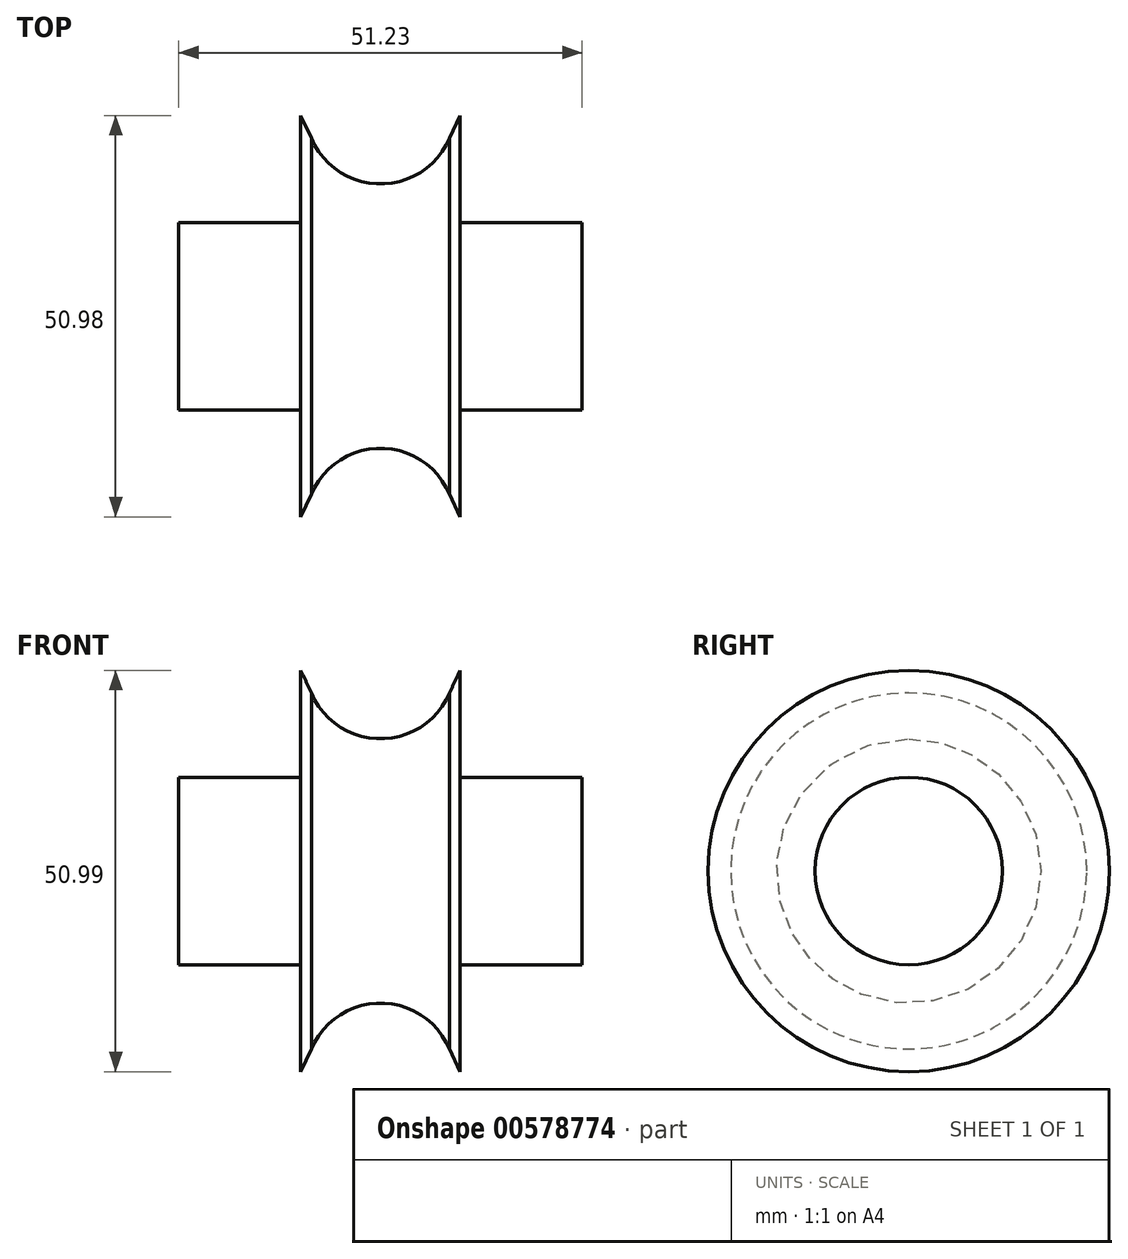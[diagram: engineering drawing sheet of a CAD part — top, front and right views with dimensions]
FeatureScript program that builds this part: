
annotation { "Feature Type Name" : "Feature", "Feature Type Description" : "" }
export const myFeature = defineFeature(function(context is Context, id is Id, definition is map)
    precondition{}
    {
        {
            var Q0;
            Q0=qCreatedBy(makeId("Front.planeOp"),FACE);
            var sketch = newSketch(context, id + "F0", { "sketchPlane" : qUnion([Q0])});
            skLineSegment(sketch, "E0", {"start": v(-30.72, 23.59) * mm, "end": v(-30.72, -1.9) * mm});
            skLineSegment(sketch, "E1", {"start": v(-30.72, 10) * mm, "end": v(-46.21, 10) * mm});
            skLineSegment(sketch, "E2", {"start": v(-46.21, 10) * mm, "end": v(-46.21, -1.9) * mm});
            skLineSegment(sketch, "E3", {"start": v(-30.72, 23.59) * mm, "end": v(-29.38, 20.71) * mm});
            skLineSegment(sketch, "E4.MirrorCS", {"start": v(-10.48, 23.59) * mm, "end": v(-11.82, 20.71) * mm});
            skArc(sketch, "E5", {"start": v(-29.38, 20.71) * mm, "mid": v(-20.6, 14.89) * mm, "end": v(-11.82, 20.71) * mm});
            skLineSegment(sketch, "E6", {"start": v(-20.6, 35.96) * mm, "end": v(-20.6, -7.2) * mm, "construction": true});
            skLineSegment(sketch, "E7.MirrorCS", {"start": v(-10.48, 23.59) * mm, "end": v(-10.48, -1.9) * mm});
            skLineSegment(sketch, "E8.MirrorCS", {"start": v(-10.48, 10) * mm, "end": v(5.02, 10) * mm});
            skLineSegment(sketch, "E9.MirrorCS", {"start": v(5.02, 10) * mm, "end": v(5.02, -1.9) * mm});
            skLineSegment(sketch, "E10", {"start": v(-55.4, -1.9) * mm, "end": v(15.86, -1.9) * mm, "construction": true});
            skLineSegment(sketch, "E11", {"start": v(-46.21, -1.9) * mm, "end": v(5.02, -1.9) * mm});
            skSolve(sketch);
        }
        {
            var Q0;
            Q0 = qSketchRegion(id + "F0", true);
            var Q1;
            Q1=sQuery(id+"F0.wireOp",EDGE,"E10");
            revolve(context, id + "F1", {"entities" : qUnion([Q0]), "axis" : qUnion([Q1]), "revolveType" : RevolveType.FULL});
        }
    });
